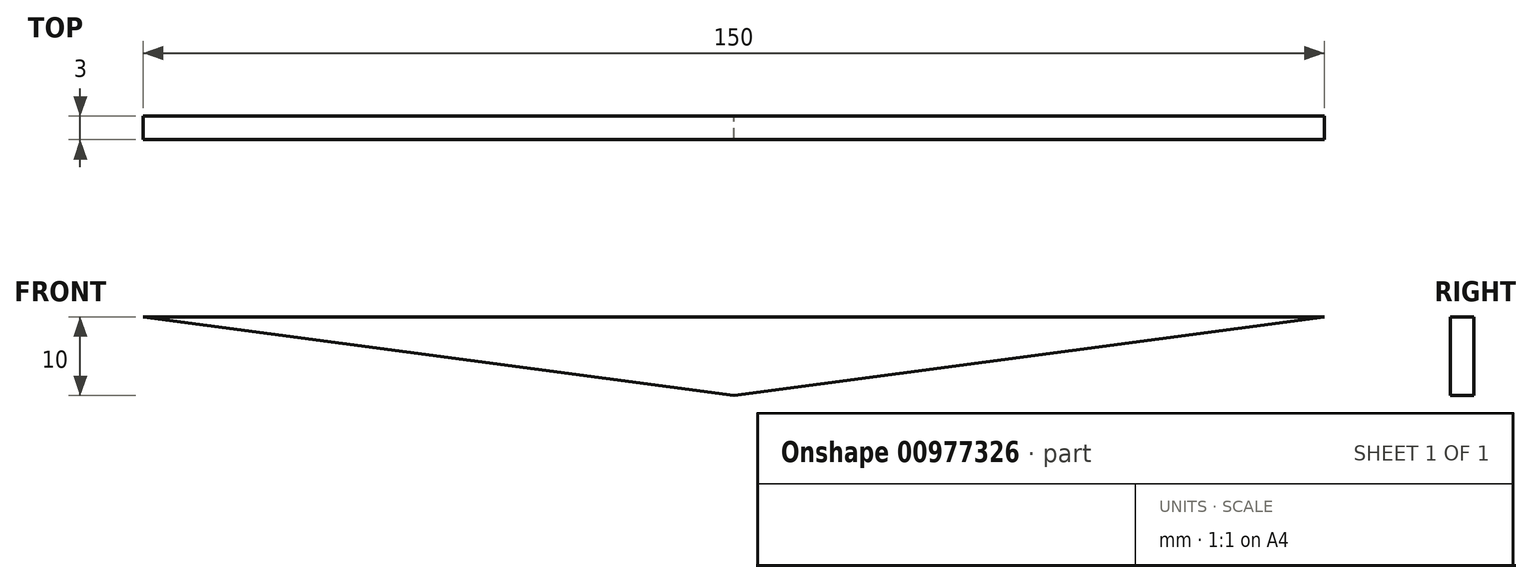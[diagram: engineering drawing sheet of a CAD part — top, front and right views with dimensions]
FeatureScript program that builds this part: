
annotation { "Feature Type Name" : "Feature", "Feature Type Description" : "" }
export const myFeature = defineFeature(function(context is Context, id is Id, definition is map)
    precondition{}
    {
        {
            var Q0;
            Q0=qCreatedBy(makeId("Front.planeOp"),FACE);
            var sketch = newSketch(context, id + "F0", { "sketchPlane" : qUnion([Q0])});
            skLineSegment(sketch, "E0", {"start": v(0, 0) * mm, "end": v(-75, 0) * mm});
            skLineSegment(sketch, "E1", {"start": v(0, 0) * mm, "end": v(75, 0) * mm});
            skLineSegment(sketch, "E2", {"start": v(75, 0) * mm, "end": v(0, -10) * mm});
            skLineSegment(sketch, "E3", {"start": v(0, -10) * mm, "end": v(-75, 0) * mm});
            skSolve(sketch);
        }
        {
            var Q0;
            Q0 = qSketchRegion(id + "F0", true);
            extrude(context, id + "F1", {"entities" : qUnion([Q0]), "depth" : 3 * mm, "offsetDistance" : 25 * mm});
        }
    });
